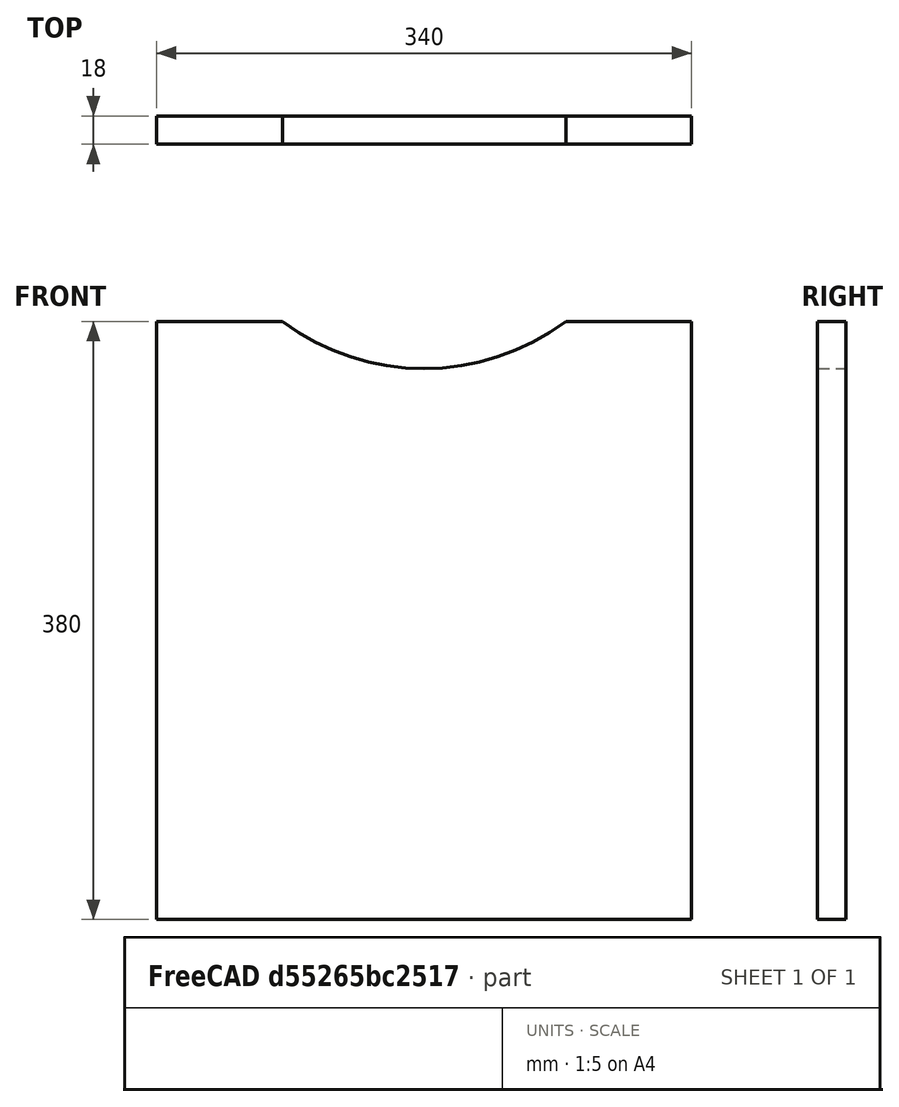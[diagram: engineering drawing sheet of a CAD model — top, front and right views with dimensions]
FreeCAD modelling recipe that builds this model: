
FCSTD DOCUMENT  (FreeCAD 0.19R21911 +2545 (Git))
Label: plyta-tylna
License: All rights reserved
LicenseURL: http://en.wikipedia.org/wiki/All_rights_reserved
objects: Sketcher::SketchObject×1, PartDesign::Pad×1, PartDesign::Body×1
note: 5 computed .brp shape members not serialized (recipe doc carries the construction recipe); baked Part::Feature solids carry a one-line shape summary decoded from their .brp

FEATURE [Sketcher::SketchObject] Sketch
  MapMode = 5
  Placement = pos=(0,0,0) rot=(1,0,0;1.5708rad)
  Support = -> [XZ_Plane]
  sketch-geometry (7):
    g0: LineSegment StartX=-170 StartY=0 StartZ=0 EndX=170 EndY=0 EndZ=0
    g1: LineSegment StartX=170 StartY=0 StartZ=0 EndX=170 EndY=380 EndZ=0
    g2: LineSegment StartX=170 StartY=380 StartZ=0 EndX=90 EndY=380 EndZ=0
    g3: LineSegment StartX=-170 StartY=380 StartZ=0 EndX=-170 EndY=0 EndZ=0
    g4: ArcOfCircle CenterX=0 CenterY=500 CenterZ=0 NormalX=0 NormalY=0 NormalZ=1 AngleXU=0 Radius=150 StartAngle=4.06889 EndAngle=5.35589
    g5: LineSegment StartX=-90 StartY=380 StartZ=0 EndX=-170 EndY=380 EndZ=0
    g6: GeomPoint X=0 Y=350 Z=0
  constraints (19):
    c: Coincident(g0,g1)
    c: Coincident(g1,g2)
    c: Coincident(g5,g3)
    c: Coincident(g3,g0)
    c: Horizontal(g0)
    c: Vertical(g1)
    c: Vertical(g3)
    c: PointOnObject(g0,g-1)
    c: Symmetric(g1,g5,g-2)
    c: DistanceY(g1,g1) = 380
    c: DistanceX(g0,g0) = 340
    c: Tangent(g2,g5)
    c: Coincident(g4,g5)
    c: Coincident(g4,g2)
    c: PointOnObject(g4,g-2)
    c: PointOnObject(g6,g-2)
    c: PointOnObject(g6,g4)
    c: DistanceY(g-1,g6) = 350
    c: DistanceX(g4,g2) = 180
FEATURE [PartDesign::Pad] Pad
  AllowMultiFace = false
  ClaimChildren = false
  Length = 18
  Length2 = 100
  Placement = pos=(0,0,0) rot=(1,0,0;1.5708rad)
  Profile = -> Sketch
  Suppress = false
  Type = 0
FEATURE [PartDesign::Body] Body  label="plyta-tylna"
  ExportMode = 0
  Group = -> [Sketch,Pad]
  Origin = -> Origin
  SingleSolid = true
  Tip = -> Pad
  _ExportChildren = -> [Pad]
  _GroupVersion = 1
